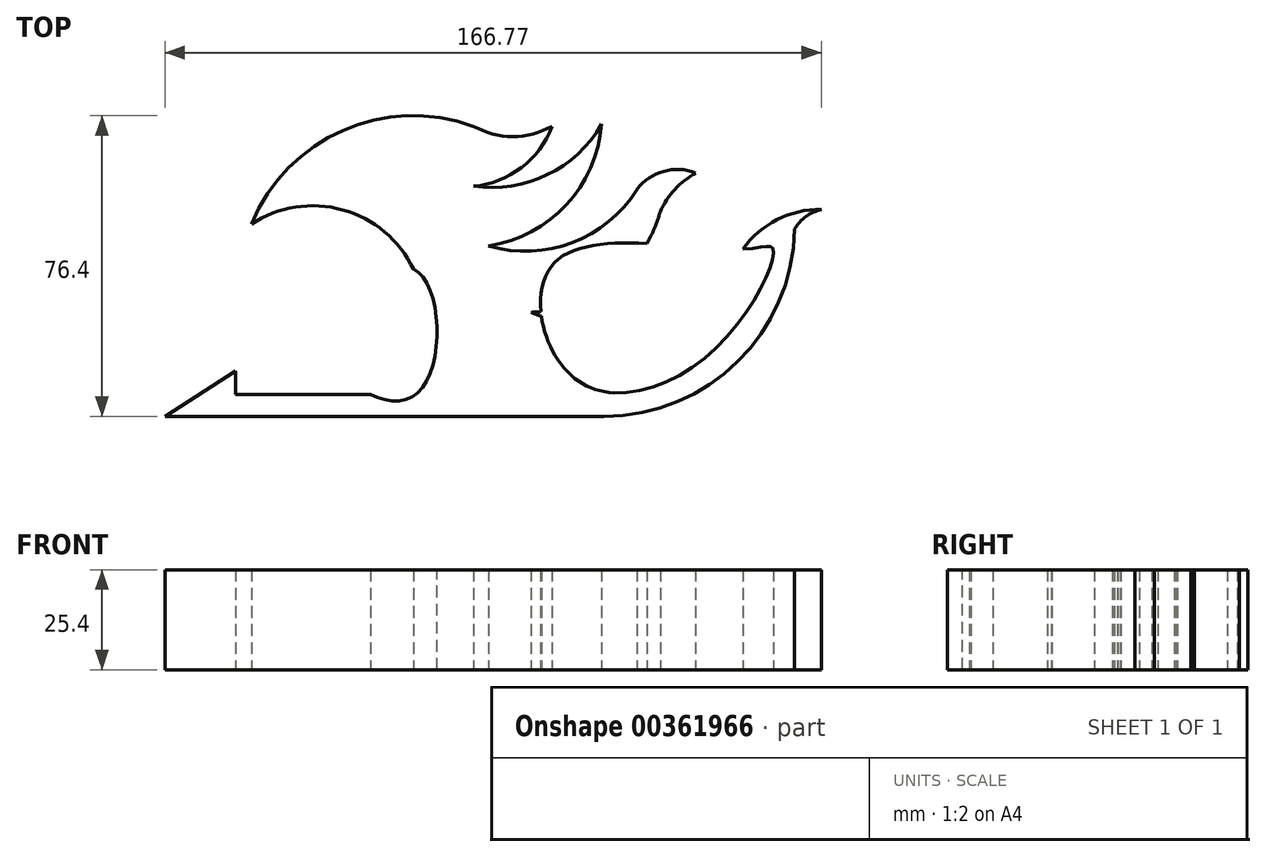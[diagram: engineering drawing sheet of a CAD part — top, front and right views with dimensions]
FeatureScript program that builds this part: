
annotation { "Feature Type Name" : "Feature", "Feature Type Description" : "" }
export const myFeature = defineFeature(function(context is Context, id is Id, definition is map)
    precondition{}
    {
        {
            var Q0;
            Q0=qCreatedBy(makeId("Top.planeOp"),FACE);
            var sketch = newSketch(context, id + "F0", { "sketchPlane" : qUnion([Q0])});
            skPoint(sketch, "E0.middle", {"position": v(0, 0) * mm});
            skArc(sketch, "E1", {"start": v(-15.33, 20.95) * mm, "mid": v(-33.32, 36.03) * mm, "end": v(-56.5, 32.36) * mm});
            skLineSegment(sketch, "E2", {"start": v(-15.33, 21.23) * mm, "end": v(-15.33, 20.95) * mm});
            skLineSegment(sketch, "E3", {"start": v(-26.26, -10.83) * mm, "end": v(-60.46, -10.83) * mm});
            skLineSegment(sketch, "E4", {"start": v(-60.46, -4.92) * mm, "end": v(-78.46, -16.45) * mm});
            skLineSegment(sketch, "E5", {"start": v(-78.46, -16.45) * mm, "end": v(-14.9, -16.45) * mm});
            skLineSegment(sketch, "E6", {"start": v(-60.46, -10.83) * mm, "end": v(-60.46, -4.92) * mm});
            skLineSegment(sketch, "E7", {"start": v(-14.9, -16.45) * mm, "end": v(33.04, -16.45) * mm});
            skArc(sketch, "E8", {"start": v(33.04, -16.45) * mm, "mid": v(67.02, -2.56) * mm, "end": v(81.53, 31.15) * mm});
            skArc(sketch, "E9", {"start": v(88.3, 36.14) * mm, "mid": v(84.41, 34.34) * mm, "end": v(81.53, 31.15) * mm});
            skArc(sketch, "E10", {"start": v(88.3, 36.14) * mm, "mid": v(77.09, 33.52) * mm, "end": v(68.34, 26.01) * mm});
            skFitSpline(sketch, "E11", {"points": [v(68.34, 26.01) * mm, v(76.07, 26.01) * mm, v(60.6, 0) * mm, v(25.73, -6.9) * mm, v(20.81, 22.92) * mm, v(68.34, 26.01) * mm]});
            skArc(sketch, "E12.filletArc", {"start": v(31.08, 0) * mm, "mid": v(30.07, -6.6) * mm, "end": v(35.52, -10.45) * mm});
            skPoint(sketch, "E13.orphan", {"position": v(20.1, 0) * mm});
            skArc(sketch, "E14", {"start": v(0, 57.23) * mm, "mid": v(-33.26, 56.18) * mm, "end": v(-56.5, 32.36) * mm});
            skArc(sketch, "E15", {"start": v(0, 57.23) * mm, "mid": v(9.91, 54.66) * mm, "end": v(19.83, 57.23) * mm});
            skArc(sketch, "E16", {"start": v(0, 42.04) * mm, "mid": v(12.12, 46.76) * mm, "end": v(19.83, 57.23) * mm});
            skArc(sketch, "E17", {"start": v(0, 42.04) * mm, "mid": v(18.66, 44.93) * mm, "end": v(32.48, 57.8) * mm});
            skArc(sketch, "E18", {"start": v(14.48, 9.98) * mm, "mid": v(36.69, 9.55) * mm, "end": v(53.01, 24.6) * mm});
            skArc(sketch, "E19", {"start": v(69.62, 35.58) * mm, "mid": v(60.07, 31.97) * mm, "end": v(53.01, 24.6) * mm});
            skArc(sketch, "E20", {"start": v(69.62, 35.58) * mm, "mid": v(64.31, 30) * mm, "end": v(62.01, 22.64) * mm});
            skArc(sketch, "E21", {"start": v(31.08, 0) * mm, "mid": v(49.52, 7.26) * mm, "end": v(62.01, 22.64) * mm});
            skPoint(sketch, "E22.end.orphan", {"position": v(33.04, 35.58) * mm});
            skPoint(sketch, "E23.start.orphan", {"position": v(0, 26.86) * mm});
            skArc(sketch, "E24", {"start": v(3.8, 26.86) * mm, "mid": v(23.53, 37.33) * mm, "end": v(32.48, 57.8) * mm});
            skArc(sketch, "E25", {"start": v(3.8, 26.86) * mm, "mid": v(25.06, 27.67) * mm, "end": v(41.48, 41.2) * mm});
            skArc(sketch, "E26", {"start": v(56.39, 45.42) * mm, "mid": v(48.23, 45.8) * mm, "end": v(41.48, 41.2) * mm});
            skArc(sketch, "E27", {"start": v(56.39, 45.42) * mm, "mid": v(51.1, 41.21) * mm, "end": v(47.39, 35.58) * mm});
            skArc(sketch, "E28", {"start": v(14.48, 9.98) * mm, "mid": v(35.13, 17.4) * mm, "end": v(47.39, 35.58) * mm});
            skFitSpline(sketch, "E29", {"points": [v(-15.33, 20.95) * mm, v(-34.17, 0) * mm, v(-14.63, -10.83) * mm, v(-15.33, 20.95) * mm]});
            skSolve(sketch);
        }
        {
            var Q0;
            Q0=makeQuery(id+"F0.imprint","IMPRINT",FACE,{"disambiguationData":[TD([[makeQuery(id+"F0.imprint","IMPRINT",EDGE,{"derivedFrom":sQuery(id+"F0.wireOp",EDGE,"E1")}),-1.0]])]});
            extrude(context, id + "F1", {"entities" : qUnion([Q0]), "depth" : 25.4 * mm});
        }
    });
